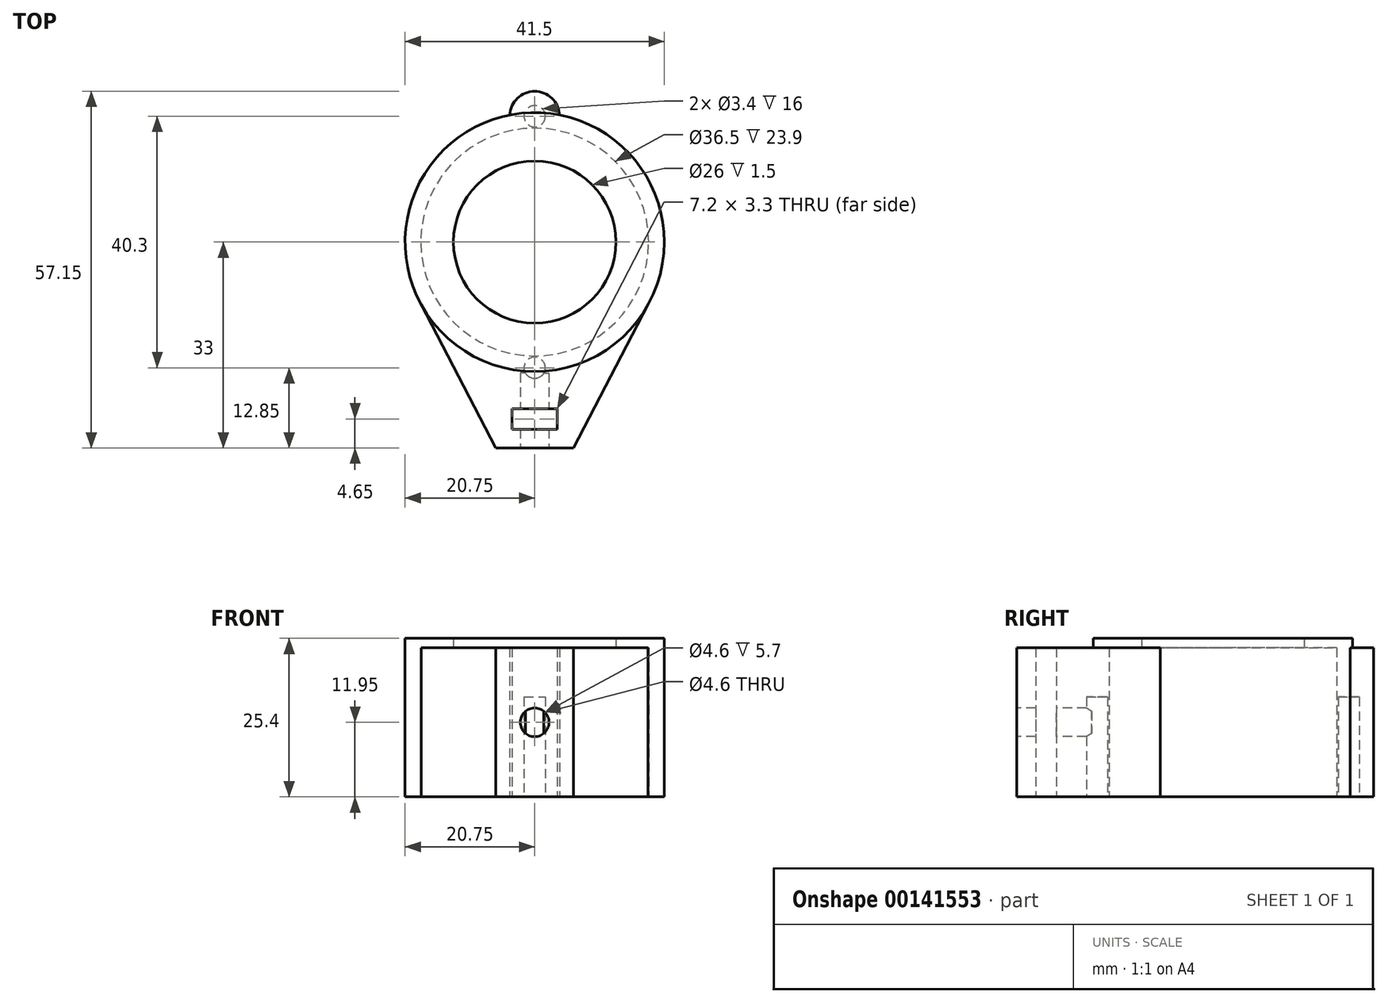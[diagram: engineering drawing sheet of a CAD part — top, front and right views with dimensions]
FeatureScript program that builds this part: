
annotation { "Feature Type Name" : "Feature", "Feature Type Description" : "" }
export const myFeature = defineFeature(function(context is Context, id is Id, definition is map)
    precondition{}
    {
        {
            var Q0;
            Q0=qCreatedBy(makeId("Top.planeOp"),FACE);
            var sketch = newSketch(context, id + "F0", { "sketchPlane" : qUnion([Q0])});
            skCircle(sketch, "E0", {"center": v(0, 0) * mm, "radius": 18.25 * mm});
            skArc(sketch, "E1", {"start": v(18.18, -10) * mm, "mid": v(18.8, 8.78) * mm, "end": v(4, 20.36) * mm});
            skLineSegment(sketch, "E2", {"start": v(-6.25, -33) * mm, "end": v(6.25, -33) * mm});
            skLineSegment(sketch, "E3", {"start": v(6.25, -33) * mm, "end": v(18.18, -10) * mm});
            skLineSegment(sketch, "E4", {"start": v(-6.25, -33) * mm, "end": v(-18.18, -10) * mm});
            skArc(sketch, "E5", {"start": v(4, 20.36) * mm, "mid": v(0, 24.15) * mm, "end": v(-4, 20.36) * mm});
            skArc(sketch, "E6.trimOffspring", {"start": v(-4, 20.36) * mm, "mid": v(-18.8, 8.78) * mm, "end": v(-18.18, -10) * mm});
            skLineSegment(sketch, "E7.bottom", {"start": v(-3.6, -26.7) * mm, "end": v(3.6, -26.7) * mm});
            skLineSegment(sketch, "E7.top", {"start": v(-3.6, -30) * mm, "end": v(3.6, -30) * mm});
            skLineSegment(sketch, "E7.left", {"start": v(-3.6, -26.7) * mm, "end": v(-3.6, -30) * mm});
            skLineSegment(sketch, "E7.right", {"start": v(3.6, -26.7) * mm, "end": v(3.6, -30) * mm});
            skSolve(sketch);
        }
        {
            var Q0;
            Q0 = qSketchRegion(id + "F0", true);
            extrude(context, id + "F1", {"entities" : qUnion([Q0]), "depth" : 23.9 * mm});
        }
        {
            var Q0;
            Q0=makeQuery(id+"F1.opExtrude","CAP_FACE",FACE,{"disambiguationData":[OSD([sQuery(id+"F0.wireOp",EDGE,"E0"),sQuery(id+"F0.wireOp",EDGE,"E1"),sQuery(id+"F0.wireOp",EDGE,"E2"),sQuery(id+"F0.wireOp",EDGE,"E3"),sQuery(id+"F0.wireOp",EDGE,"E4"),sQuery(id+"F0.wireOp",EDGE,"E5"),sQuery(id+"F0.wireOp",EDGE,"E6.trimOffspring"),sQuery(id+"F0.wireOp",EDGE,"E7.bottom"),sQuery(id+"F0.wireOp",EDGE,"E7.top"),sQuery(id+"F0.wireOp",EDGE,"E7.left"),sQuery(id+"F0.wireOp",EDGE,"E7.right")])],"isStart":false});
            var sketch = newSketch(context, id + "F2", { "sketchPlane" : qUnion([Q0])});
            skCircle(sketch, "E8", {"center": v(0, 0) * mm, "radius": 20.75 * mm});
            skCircle(sketch, "E9", {"center": v(0, 0) * mm, "radius": 13 * mm});
            skSolve(sketch);
        }
        {
            var Q0;
            Q0 = qSketchRegion(id + "F2", true);
            extrude(context, id + "F3", {"entities" : qUnion([Q0]), "operationType" : NewBodyOperationType.ADD, "depth" : 1.5 * mm});
        }
        {
            var Q0;
            Q0=makeQuery(id+"F1.opExtrude","CAP_FACE",FACE,{"disambiguationData":[OSD([sQuery(id+"F0.wireOp",EDGE,"E0"),sQuery(id+"F0.wireOp",EDGE,"E1"),sQuery(id+"F0.wireOp",EDGE,"E2"),sQuery(id+"F0.wireOp",EDGE,"E3"),sQuery(id+"F0.wireOp",EDGE,"E4"),sQuery(id+"F0.wireOp",EDGE,"E5"),sQuery(id+"F0.wireOp",EDGE,"E6.trimOffspring"),sQuery(id+"F0.wireOp",EDGE,"E7.bottom"),sQuery(id+"F0.wireOp",EDGE,"E7.top"),sQuery(id+"F0.wireOp",EDGE,"E7.left"),sQuery(id+"F0.wireOp",EDGE,"E7.right")])],"isStart":true});
            var sketch = newSketch(context, id + "F4", { "sketchPlane" : qUnion([Q0])});
            skCircle(sketch, "E10", {"center": v(0, 20.15) * mm, "radius": 1.7 * mm});
            skCircle(sketch, "E11", {"center": v(0, -20.15) * mm, "radius": 1.7 * mm});
            skSolve(sketch);
        }
        {
            var Q0;
            Q0 = qSketchRegion(id + "F4", true);
            extrude(context, id + "F5", {"entities" : qUnion([Q0]), "operationType" : NewBodyOperationType.REMOVE, "oppositeDirection" : true, "depth" : 16 * mm});
        }
        {
            var Q0;
            Q0=makeQuery(id+"F1.opExtrude","SWEPT_FACE",FACE,{"disambiguationData":[OSD([sQuery(id+"F0.wireOp",EDGE,"E2")])]});
            var sketch = newSketch(context, id + "F6", { "sketchPlane" : qUnion([Q0])});
            skCircle(sketch, "E12", {"center": v(0, 11.95) * mm, "radius": 2.3 * mm});
            skPoint(sketch, "E12.centerSnap0", {"position": v(-6.25, 11.95) * mm});
            skSolve(sketch);
        }
        {
            var Q0;
            Q0 = qSketchRegion(id + "F6", true);
            extrude(context, id + "F7", {"entities" : qUnion([Q0]), "operationType" : NewBodyOperationType.REMOVE, "oppositeDirection" : true, "depth" : 12 * mm});
        }
    });
